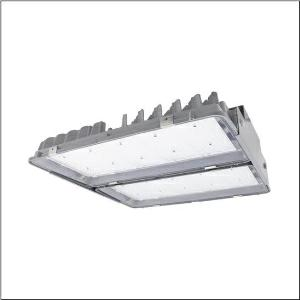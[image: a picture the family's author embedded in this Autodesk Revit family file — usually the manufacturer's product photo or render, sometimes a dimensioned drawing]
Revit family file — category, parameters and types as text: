
# Revit family: highbay_11xtreme_51hf82db4vma
name_source: partatom
category: Lighting Fixtures
units: mm (PartAtom-declared; Revit-internal decimal feet)

## family parameters
Cut with Voids When Loaded = No
Host = Face
Light Source = No
Part Type = Normal
Room Calculation Point = No
Round Connector Dimension = Use Diameter
Shared = No

## types (1)
- --- (1 x LED, 68500 lm, 380.3 W, 4000K)
    Apparent Load = 380 VA
    CIE Flux Codes = 84 96 100 100 100
    Color Rendering = 80
    Color Temperature = 4000K
    Default Elevation = 1800 mm
    Description = Highbay 11Xtreme, LED high bay luminaire, primary light control with lens, of PMMA, primary optical cover: cover, of toughened safety glass, light emission: direct distribution, primary light characteristic: symmetric, installation type: suspended mounting, surface-mounted, 2x LED module,for 1x 2x LED, rated luminous flux: 68.500lm, luminous efficacy: 180lm/W, light colour: 840, colour temperature: 4000K, with cable H07RN-F 5x 1.5mm², mains connection: 220..240V, AC, 50/60Hz, cable length: 1,5m, rated input power: 380W, luminaire housing, of diecast aluminium, partly coated, silver, length: 595mm, width: 560mm, height: 195mm, protection rating (complete): IP66, insulation class (complete): insulation class I (protective earthing), certification: CE, ENEC, UKCA, protection symbol: D, ball protection: ball impact resistant according to DIN VDE 0710 part 13 (with chain suspension), impact resistance: IK08, permissible operating ambient temperature: -25..+45°C, reducing of maximum allowable ambient temperature of 5°C with ceiling mounting, packaging unit: 1 piece
    Height = 157 mm
    Lamp = 1 x LED
    Lamp Light Flux = 68500 lm
    Lamp Power = 380.3 W
    Lamp count = 1
    Length = 593 mm
    Luminous efficacy = 180 lm/W
    Manufacturer = Siteco
    ModVariant = No
    Model = 51HF82DB4VMA
    Mounting Place = Ceiling
    Mounting Type = Pendant
    Number of Poles = 1
    OnlyDefault = Yes
    Power Factor = 1
    Product Name = Highbay 11Xtreme
    Product group = LED high bay luminaire
    ProductGroupID = 903
    Protection Class = Protection class I
    Protection Degree = IP 66
    RLX_Detail_Level = 1
    RLX_Emergency_Light_Flux = 0 lm
    RLX_Emergency_Type = 0
    RLX_Emergency_Type_DB = No
    RlxData = <blob elided: 34345 chars, md5=a97aeedd>
    Socket = socket
    Standby Power = 0 W
    System Light Flux = 68500 lm
    System Power = 380 W
    Type Comments = factory setting: luminous flux: 100 % | dim-lin: 254 | 1257 mA
    Type Image = l_1258340.jpg
    URL = http://relux.com
    VarID = @adj_052431
    Voltage = 0 V
    Weight = 0.00 kg
    Width = 568 mm

## geometry (parser evidence)
native form markers: Blend x4, Sweep x10
no freeform markers — native parametric forms only
